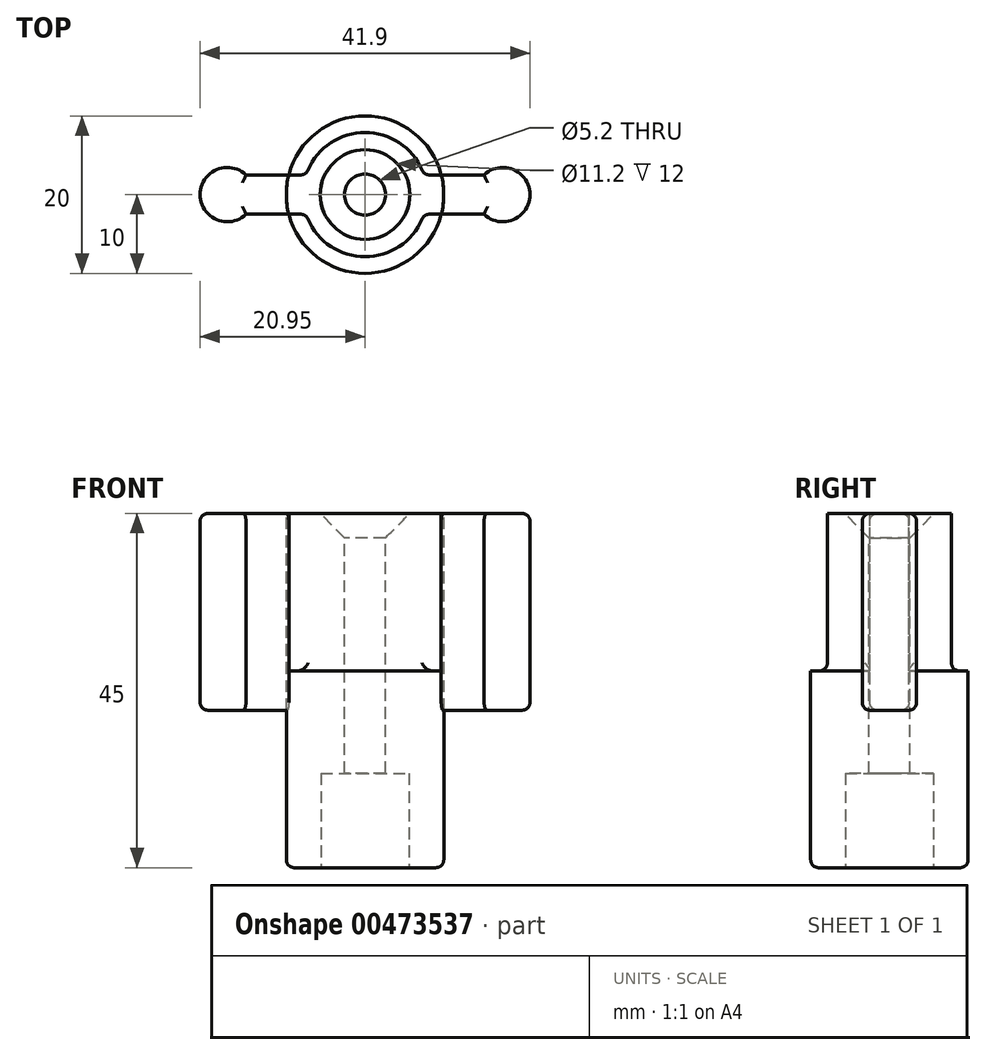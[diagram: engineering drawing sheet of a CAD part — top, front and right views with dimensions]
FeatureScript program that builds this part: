
annotation { "Feature Type Name" : "Feature", "Feature Type Description" : "" }
export const myFeature = defineFeature(function(context is Context, id is Id, definition is map)
    precondition{}
    {
        {
            var Q0;
            Q0=qCreatedBy(makeId("Top.planeOp"),FACE);
            var sketch = newSketch(context, id + "F0", { "sketchPlane" : qUnion([Q0])});
            skCircle(sketch, "E0", {"center": v(0, 0) * mm, "radius": 10 * mm});
            skSolve(sketch);
        }
        {
            var Q0;
            Q0=makeQuery(id+"F0.imprint","IMPRINT",FACE,{"disambiguationData":[TD([[makeQuery(id+"F0.imprint","IMPRINT",EDGE,{"derivedFrom":sQuery(id+"F0.wireOp",EDGE,"E0")}),1.0]])]});
            extrude(context, id + "F1", {"entities" : qUnion([Q0]), "depth" : 45 * mm, "offsetDistance" : 25 * mm, "symmetric" : true});
        }
        {
            var Q0;
            Q0=makeQuery(id+"F1.opExtrude","CAP_FACE",FACE,{"disambiguationData":[OSD([sQuery(id+"F0.wireOp",EDGE,"E0")])],"isStart":false});
            var sketch = newSketch(context, id + "F2", { "sketchPlane" : qUnion([Q0])});
            skLineSegment(sketch, "E1.bottom", {"start": v(17.5, -2.5) * mm, "end": v(-17.5, -2.5) * mm});
            skLineSegment(sketch, "E1.top", {"start": v(17.5, 2.5) * mm, "end": v(-17.5, 2.5) * mm});
            skLineSegment(sketch, "E1.left", {"start": v(17.5, -2.5) * mm, "end": v(17.5, 2.5) * mm});
            skLineSegment(sketch, "E1.right", {"start": v(-17.5, -2.5) * mm, "end": v(-17.5, 2.5) * mm});
            skPoint(sketch, "E1.middle", {"position": v(0, 0) * mm});
            skCircle(sketch, "E2", {"center": v(0, 0) * mm, "radius": 7.89 * mm});
            skCircle(sketch, "E3", {"center": v(-17.5, 0) * mm, "radius": 3.45 * mm});
            skCircle(sketch, "E4", {"center": v(17.5, 0) * mm, "radius": 3.45 * mm});
            skSolve(sketch);
        }
        {
            var Q0;
            {var subQ0=sQuery(id+"F2.wireOp",EDGE,"E2");var subQ1=sQuery(id+"F2.wireOp",EDGE,"E1.top");var subQ2=makeQuery(id+"F2.imprint","INTERSECT",VERTEX,{"disambiguationData":[OD(0.0)],"derivedFrom":[subQ1,subQ0]});Q0=makeQuery(id+"F2.imprint","IMPRINT",FACE,{"disambiguationData":[TD([[makeQuery(id+"F2.imprint","IMPRINT",EDGE,{"disambiguationData":[TD([[subQ2,1.0]])],"derivedFrom":subQ1}),-1.0]])]});}
            var Q1;
            {var subQ0=sQuery(id+"F2.wireOp",EDGE,"E2");var subQ1=sQuery(id+"F2.wireOp",EDGE,"E1.bottom");var subQ2=makeQuery(id+"F2.imprint","INTERSECT",VERTEX,{"disambiguationData":[OD(0.0)],"derivedFrom":[subQ1,subQ0]});Q1=makeQuery(id+"F2.imprint","IMPRINT",FACE,{"disambiguationData":[TD([[makeQuery(id+"F2.imprint","IMPRINT",EDGE,{"disambiguationData":[TD([[subQ2,1.0]])],"derivedFrom":subQ1}),1.0]])]});}
            extrude(context, id + "F3", {"entities" : qUnion([Q0, Q1]), "operationType" : NewBodyOperationType.REMOVE, "oppositeDirection" : true, "depth" : 20 * mm, "offsetDistance" : 25 * mm});
        }
        {
            var Q0;
            {var subQ0=sQuery(id+"F2.wireOp",EDGE,"E1.left");Q0=makeQuery(id+"F2.imprint","IMPRINT",FACE,{"disambiguationData":[TD([[makeQuery(id+"F2.imprint","IMPRINT",EDGE,{"derivedFrom":subQ0}),1.0]])]});}
            var Q1;
            {var subQ0=sQuery(id+"F2.wireOp",EDGE,"E1.right");Q1=makeQuery(id+"F2.imprint","IMPRINT",FACE,{"disambiguationData":[TD([[makeQuery(id+"F2.imprint","IMPRINT",EDGE,{"derivedFrom":subQ0}),-1.0]])]});}
            var Q2;
            {var subQ0=sQuery(id+"F2.wireOp",EDGE,"E4");var subQ1=sQuery(id+"F2.wireOp",EDGE,"E1.bottom");var subQ2=makeQuery(id+"F2.imprint","INTERSECT",VERTEX,{"derivedFrom":[subQ1,subQ0]});Q2=makeQuery(id+"F2.imprint","IMPRINT",FACE,{"disambiguationData":[TD([[makeQuery(id+"F2.imprint","IMPRINT",EDGE,{"disambiguationData":[TD([[subQ2,-1.0]])],"derivedFrom":subQ1}),-1.0]])]});}
            var Q3;
            {var subQ0=sQuery(id+"F2.wireOp",EDGE,"E1.left");Q3=makeQuery(id+"F2.imprint","IMPRINT",FACE,{"disambiguationData":[TD([[makeQuery(id+"F2.imprint","IMPRINT",EDGE,{"derivedFrom":subQ0}),-1.0]])]});}
            var Q4;
            {var subQ0=sQuery(id+"F2.wireOp",EDGE,"E3");var subQ1=sQuery(id+"F2.wireOp",EDGE,"E1.bottom");var subQ2=makeQuery(id+"F2.imprint","INTERSECT",VERTEX,{"derivedFrom":[subQ1,subQ0]});Q4=makeQuery(id+"F2.imprint","IMPRINT",FACE,{"disambiguationData":[TD([[makeQuery(id+"F2.imprint","IMPRINT",EDGE,{"disambiguationData":[TD([[subQ2,1.0]])],"derivedFrom":subQ1}),-1.0]])]});}
            var Q5;
            {var subQ0=sQuery(id+"F2.wireOp",EDGE,"E1.right");Q5=makeQuery(id+"F2.imprint","IMPRINT",FACE,{"disambiguationData":[TD([[makeQuery(id+"F2.imprint","IMPRINT",EDGE,{"derivedFrom":subQ0}),1.0]])]});}
            extrude(context, id + "F4", {"entities" : qUnion([Q0, Q1, Q2, Q3, Q4, Q5]), "oppositeDirection" : true, "depth" : 25 * mm, "offsetDistance" : 25 * mm});
        }
        {
            var Q0;
            {var subQ0=sQuery(id+"F2.wireOp",EDGE,"E1.top");Q0=makeQuery(id+"F4.opExtrude","CAP_EDGE",EDGE,{"disambiguationData":[OSD([subQ0]),TDD([makeQuery(id+"F2.imprint","IMPRINT",EDGE,{"disambiguationData":[TD([[makeQuery(id+"F2.imprint","INTERSECT",VERTEX,{"derivedFrom":[subQ0,sQuery(id+"F2.wireOp",EDGE,"E3")]}),1.0]])],"derivedFrom":subQ0})])],"isStart":true});}
            var Q1;
            {var subQ0=sQuery(id+"F2.wireOp",EDGE,"E2");var subQ1=sQuery(id+"F2.wireOp",EDGE,"E1.top");Q1=makeQuery(id+"F3.boolean.opBoolean","COPY",EDGE,{"derivedFrom":makeQuery(id+"F3.opExtrude","CAP_EDGE",EDGE,{"disambiguationData":[OSD([subQ0]),TDD([makeQuery(id+"F2.imprint","IMPRINT",EDGE,{"disambiguationData":[TD([[makeQuery(id+"F2.imprint","INTERSECT",VERTEX,{"disambiguationData":[OD(0.0)],"derivedFrom":[subQ1,subQ0]}),-1.0]])],"derivedFrom":subQ0})])],"isStart":true})});}
            var Q2;
            {var subQ0=sQuery(id+"F2.wireOp",EDGE,"E2");var subQ1=sQuery(id+"F2.wireOp",EDGE,"E1.bottom");Q2=makeQuery(id+"F3.boolean.opBoolean","COPY",EDGE,{"derivedFrom":makeQuery(id+"F3.opExtrude","CAP_EDGE",EDGE,{"disambiguationData":[OSD([subQ0]),TDD([makeQuery(id+"F2.imprint","IMPRINT",EDGE,{"disambiguationData":[TD([[makeQuery(id+"F2.imprint","INTERSECT",VERTEX,{"disambiguationData":[OD(0.0)],"derivedFrom":[subQ1,subQ0]}),1.0]])],"derivedFrom":subQ0})])],"isStart":true})});}
            var Q3;
            {var subQ0=sQuery(id+"F2.wireOp",EDGE,"E1.bottom");Q3=makeQuery(id+"F3.boolean.opBoolean","COPY",EDGE,{"derivedFrom":makeQuery(id+"F3.opExtrude","CAP_EDGE",EDGE,{"disambiguationData":[OSD([subQ0]),TDD([makeQuery(id+"F2.imprint","IMPRINT",EDGE,{"disambiguationData":[TD([[makeQuery(id+"F2.imprint","INTERSECT",VERTEX,{"disambiguationData":[OD(1.0)],"derivedFrom":[subQ0,sQuery(id+"F2.wireOp",EDGE,"E2")]}),-1.0]])],"derivedFrom":subQ0})])],"isStart":true})});}
            var Q4;
            {var subQ0=sQuery(id+"F2.wireOp",EDGE,"E1.bottom");Q4=makeQuery(id+"F4.opExtrude","CAP_EDGE",EDGE,{"disambiguationData":[OSD([subQ0]),TDD([makeQuery(id+"F2.imprint","IMPRINT",EDGE,{"disambiguationData":[TD([[makeQuery(id+"F2.imprint","INTERSECT",VERTEX,{"derivedFrom":[subQ0,sQuery(id+"F2.wireOp",EDGE,"E3")]}),1.0]])],"derivedFrom":subQ0})])],"isStart":true});}
            var Q5;
            {var subQ0=sQuery(id+"F2.wireOp",EDGE,"E1.bottom");Q5=makeQuery(id+"F3.boolean.opBoolean","COPY",EDGE,{"derivedFrom":makeQuery(id+"F3.opExtrude","CAP_EDGE",EDGE,{"disambiguationData":[OSD([subQ0]),TDD([makeQuery(id+"F2.imprint","IMPRINT",EDGE,{"disambiguationData":[TD([[makeQuery(id+"F2.imprint","INTERSECT",VERTEX,{"disambiguationData":[OD(0.0)],"derivedFrom":[subQ0,sQuery(id+"F2.wireOp",EDGE,"E2")]}),1.0]])],"derivedFrom":subQ0})])],"isStart":true})});}
            var Q6;
            {var subQ0=sQuery(id+"F2.wireOp",EDGE,"E1.bottom");Q6=makeQuery(id+"F4.opExtrude","CAP_EDGE",EDGE,{"disambiguationData":[OSD([subQ0]),TDD([makeQuery(id+"F2.imprint","IMPRINT",EDGE,{"disambiguationData":[TD([[makeQuery(id+"F2.imprint","INTERSECT",VERTEX,{"derivedFrom":[subQ0,sQuery(id+"F2.wireOp",EDGE,"E4")]}),-1.0]])],"derivedFrom":subQ0})])],"isStart":true});}
            var Q7;
            {var subQ0=sQuery(id+"F2.wireOp",EDGE,"E1.top");Q7=makeQuery(id+"F3.boolean.opBoolean","COPY",EDGE,{"derivedFrom":makeQuery(id+"F3.opExtrude","CAP_EDGE",EDGE,{"disambiguationData":[OSD([subQ0]),TDD([makeQuery(id+"F2.imprint","IMPRINT",EDGE,{"disambiguationData":[TD([[makeQuery(id+"F2.imprint","INTERSECT",VERTEX,{"disambiguationData":[OD(1.0)],"derivedFrom":[subQ0,sQuery(id+"F2.wireOp",EDGE,"E2")]}),-1.0]])],"derivedFrom":subQ0})])],"isStart":true})});}
            var Q8;
            {var subQ0=sQuery(id+"F2.wireOp",EDGE,"E1.top");Q8=makeQuery(id+"F3.boolean.opBoolean","COPY",EDGE,{"derivedFrom":makeQuery(id+"F3.opExtrude","CAP_EDGE",EDGE,{"disambiguationData":[OSD([subQ0]),TDD([makeQuery(id+"F2.imprint","IMPRINT",EDGE,{"disambiguationData":[TD([[makeQuery(id+"F2.imprint","INTERSECT",VERTEX,{"disambiguationData":[OD(0.0)],"derivedFrom":[subQ0,sQuery(id+"F2.wireOp",EDGE,"E2")]}),1.0]])],"derivedFrom":subQ0})])],"isStart":true})});}
            var Q9;
            {var subQ0=sQuery(id+"F2.wireOp",EDGE,"E1.top");Q9=makeQuery(id+"F4.opExtrude","CAP_EDGE",EDGE,{"disambiguationData":[OSD([subQ0]),TDD([makeQuery(id+"F2.imprint","IMPRINT",EDGE,{"disambiguationData":[TD([[makeQuery(id+"F2.imprint","INTERSECT",VERTEX,{"derivedFrom":[subQ0,sQuery(id+"F2.wireOp",EDGE,"E4")]}),-1.0]])],"derivedFrom":subQ0})])],"isStart":true});}
            var Q10;
            {var subQ0=sQuery(id+"F2.wireOp",EDGE,"E2");var subQ1=sQuery(id+"F2.wireOp",EDGE,"E1.top");Q10=makeQuery(id+"F3.boolean.opBoolean","COPY",EDGE,{"derivedFrom":makeQuery(id+"F3.opExtrude","SWEPT_EDGE",EDGE,{"disambiguationData":[OSD([subQ1,subQ0]),TDD([makeQuery(id+"F2.imprint","INTERSECT",VERTEX,{"disambiguationData":[OD(0.0)],"derivedFrom":[subQ1,subQ0]})])]})});}
            var Q11;
            {var subQ0=sQuery(id+"F2.wireOp",EDGE,"E2");var subQ1=sQuery(id+"F2.wireOp",EDGE,"E1.top");Q11=makeQuery(id+"F3.boolean.opBoolean","COPY",EDGE,{"derivedFrom":makeQuery(id+"F3.opExtrude","SWEPT_EDGE",EDGE,{"disambiguationData":[OSD([subQ1,subQ0]),TDD([makeQuery(id+"F2.imprint","INTERSECT",VERTEX,{"disambiguationData":[OD(1.0)],"derivedFrom":[subQ1,subQ0]})])]})});}
            var Q12;
            {var subQ0=sQuery(id+"F2.wireOp",EDGE,"E2");var subQ1=sQuery(id+"F2.wireOp",EDGE,"E1.top");Q12=makeQuery(id+"F3.boolean.opBoolean","COPY",EDGE,{"derivedFrom":makeQuery(id+"F3.opExtrude","CAP_EDGE",EDGE,{"disambiguationData":[OSD([subQ0]),TDD([makeQuery(id+"F2.imprint","IMPRINT",EDGE,{"disambiguationData":[TD([[makeQuery(id+"F2.imprint","INTERSECT",VERTEX,{"disambiguationData":[OD(0.0)],"derivedFrom":[subQ1,subQ0]}),-1.0]])],"derivedFrom":subQ0})])],"isStart":false})});}
            var Q13;
            {var subQ0=sQuery(id+"F2.wireOp",EDGE,"E1.top");var subQ1=sQuery(id+"F0.wireOp",EDGE,"E0");var subQ2=makeQuery(id+"F1.opExtrude","CAP_EDGE",EDGE,{"disambiguationData":[OSD([subQ1])],"isStart":false});Q13=makeQuery(id+"F3.boolean.opBoolean","COPY",EDGE,{"derivedFrom":makeQuery(id+"F3.opExtrude","CAP_EDGE",EDGE,{"disambiguationData":[OSD([subQ1]),TDD([makeQuery(id+"F2.imprint","IMPRINT",EDGE,{"disambiguationData":[TD([[makeQuery(id+"F2.imprint","INTERSECT",VERTEX,{"disambiguationData":[OD(0.0)],"derivedFrom":[subQ2,subQ0]}),-1.0]])],"derivedFrom":subQ2})])],"isStart":false})});}
            var Q14;
            {var subQ0=sQuery(id+"F2.wireOp",EDGE,"E2");var subQ1=sQuery(id+"F2.wireOp",EDGE,"E1.bottom");Q14=makeQuery(id+"F3.boolean.opBoolean","COPY",EDGE,{"derivedFrom":makeQuery(id+"F3.opExtrude","SWEPT_EDGE",EDGE,{"disambiguationData":[OSD([subQ1,subQ0]),TDD([makeQuery(id+"F2.imprint","INTERSECT",VERTEX,{"disambiguationData":[OD(0.0)],"derivedFrom":[subQ1,subQ0]})])]})});}
            var Q15;
            {var subQ0=sQuery(id+"F2.wireOp",EDGE,"E2");var subQ1=sQuery(id+"F2.wireOp",EDGE,"E1.bottom");Q15=makeQuery(id+"F3.boolean.opBoolean","COPY",EDGE,{"derivedFrom":makeQuery(id+"F3.opExtrude","CAP_EDGE",EDGE,{"disambiguationData":[OSD([subQ0]),TDD([makeQuery(id+"F2.imprint","IMPRINT",EDGE,{"disambiguationData":[TD([[makeQuery(id+"F2.imprint","INTERSECT",VERTEX,{"disambiguationData":[OD(0.0)],"derivedFrom":[subQ1,subQ0]}),1.0]])],"derivedFrom":subQ0})])],"isStart":false})});}
            var Q16;
            {var subQ0=sQuery(id+"F2.wireOp",EDGE,"E1.bottom");var subQ1=sQuery(id+"F0.wireOp",EDGE,"E0");var subQ2=makeQuery(id+"F1.opExtrude","CAP_EDGE",EDGE,{"disambiguationData":[OSD([subQ1])],"isStart":false});Q16=makeQuery(id+"F3.boolean.opBoolean","COPY",EDGE,{"derivedFrom":makeQuery(id+"F3.opExtrude","CAP_EDGE",EDGE,{"disambiguationData":[OSD([subQ1]),TDD([makeQuery(id+"F2.imprint","IMPRINT",EDGE,{"disambiguationData":[TD([[makeQuery(id+"F2.imprint","INTERSECT",VERTEX,{"disambiguationData":[OD(0.0)],"derivedFrom":[subQ2,subQ0]}),1.0]])],"derivedFrom":subQ2})])],"isStart":false})});}
            var Q17;
            {var subQ0=sQuery(id+"F2.wireOp",EDGE,"E2");var subQ1=sQuery(id+"F2.wireOp",EDGE,"E1.bottom");Q17=makeQuery(id+"F3.boolean.opBoolean","COPY",EDGE,{"derivedFrom":makeQuery(id+"F3.opExtrude","SWEPT_EDGE",EDGE,{"disambiguationData":[OSD([subQ1,subQ0]),TDD([makeQuery(id+"F2.imprint","INTERSECT",VERTEX,{"disambiguationData":[OD(1.0)],"derivedFrom":[subQ1,subQ0]})])]})});}
            var Q18;
            {var subQ0=sQuery(id+"F2.wireOp",EDGE,"E1.bottom");Q18=makeQuery(id+"F4.opExtrude","CAP_EDGE",EDGE,{"disambiguationData":[OSD([subQ0]),TDD([makeQuery(id+"F2.imprint","IMPRINT",EDGE,{"disambiguationData":[TD([[makeQuery(id+"F2.imprint","INTERSECT",VERTEX,{"derivedFrom":[subQ0,sQuery(id+"F2.wireOp",EDGE,"E3")]}),1.0]])],"derivedFrom":subQ0})])],"isStart":false});}
            var Q19;
            {var subQ0=sQuery(id+"F2.wireOp",EDGE,"E1.top");Q19=makeQuery(id+"F4.opExtrude","CAP_EDGE",EDGE,{"disambiguationData":[OSD([subQ0]),TDD([makeQuery(id+"F2.imprint","IMPRINT",EDGE,{"disambiguationData":[TD([[makeQuery(id+"F2.imprint","INTERSECT",VERTEX,{"derivedFrom":[subQ0,sQuery(id+"F2.wireOp",EDGE,"E3")]}),1.0]])],"derivedFrom":subQ0})])],"isStart":false});}
            var Q20;
            {var subQ0=sQuery(id+"F2.wireOp",EDGE,"E1.bottom");Q20=makeQuery(id+"F4.opExtrude","CAP_EDGE",EDGE,{"disambiguationData":[OSD([subQ0]),TDD([makeQuery(id+"F2.imprint","IMPRINT",EDGE,{"disambiguationData":[TD([[makeQuery(id+"F2.imprint","INTERSECT",VERTEX,{"derivedFrom":[subQ0,sQuery(id+"F2.wireOp",EDGE,"E4")]}),-1.0]])],"derivedFrom":subQ0})])],"isStart":false});}
            var Q21;
            {var subQ0=sQuery(id+"F2.wireOp",EDGE,"E1.top");Q21=makeQuery(id+"F4.opExtrude","CAP_EDGE",EDGE,{"disambiguationData":[OSD([subQ0]),TDD([makeQuery(id+"F2.imprint","IMPRINT",EDGE,{"disambiguationData":[TD([[makeQuery(id+"F2.imprint","INTERSECT",VERTEX,{"derivedFrom":[subQ0,sQuery(id+"F2.wireOp",EDGE,"E4")]}),-1.0]])],"derivedFrom":subQ0})])],"isStart":false});}
            fillet(context, id + "F5", {"entities" : qUnion([Q0, Q1, Q2, Q3, Q4, Q5, Q6, Q7, Q8, Q9, Q10, Q11, Q12, Q13, Q14, Q15, Q16, Q17, Q18, Q19, Q20, Q21]), "radius" : 1 * mm, "allowEdgeOverflow" : false});
        }
        {
            var Q0;
            Q0=makeQuery(id+"F4.opExtrude","CAP_EDGE",EDGE,{"disambiguationData":[OSD([sQuery(id+"F2.wireOp",EDGE,"E4")])],"isStart":true});
            var Q1;
            Q1=makeQuery(id+"F4.opExtrude","CAP_EDGE",EDGE,{"disambiguationData":[OSD([sQuery(id+"F2.wireOp",EDGE,"E3")])],"isStart":true});
            var Q2;
            Q2=makeQuery(id+"F4.opExtrude","CAP_EDGE",EDGE,{"disambiguationData":[OSD([sQuery(id+"F2.wireOp",EDGE,"E3")])],"isStart":false});
            var Q3;
            Q3=makeQuery(id+"F4.opExtrude","CAP_EDGE",EDGE,{"disambiguationData":[OSD([sQuery(id+"F2.wireOp",EDGE,"E4")])],"isStart":false});
            fillet(context, id + "F6", {"entities" : qUnion([Q0, Q1, Q2, Q3]), "radius" : 1 * mm, "tangentPropagation" : true, "allowEdgeOverflow" : false});
        }
        {
            var Q0;
            Q0=sQuery(id+"F2.wireOp",VERTEX,"E1.middle");
            var Q1;
            Q1=makeQuery(id+"F1.opExtrude","SWEPT_BODY",BODY,{"disambiguationData":[OSD([sQuery(id+"F0.wireOp",EDGE,"E0")])]});
            hole(context, id + "F7", {"style" : HoleStyle.C_SINK, "endStyle" : HoleEndStyle.THROUGH, "holeDiameter" : 5.2 * mm, "cSinkDiameter" : 11.4 * mm, "cSinkAngle" : 90 * degree, "majorDiameter" : 5 * mm, "isTappedThrough" : true, "tappedDepth" : 12 * mm, "tapClearance" : 3, "locations" : qUnion([Q0]), "scope" : qUnion([Q1])});
        }
        {
            var Q0;
            Q0=makeQuery(id+"F1.opExtrude","CAP_FACE",FACE,{"disambiguationData":[OSD([sQuery(id+"F0.wireOp",EDGE,"E0")])],"isStart":true});
            var sketch = newSketch(context, id + "F8", { "sketchPlane" : qUnion([Q0])});
            skCircle(sketch, "E5", {"center": v(0, 0) * mm, "radius": 5.6 * mm});
            skSolve(sketch);
        }
        {
            var Q0;
            Q0=makeQuery(id+"F8.imprint","IMPRINT",FACE,{"disambiguationData":[TD([[makeQuery(id+"F8.imprint","IMPRINT",EDGE,{"derivedFrom":sQuery(id+"F8.wireOp",EDGE,"E5")}),1.0]])]});
            extrude(context, id + "F9", {"entities" : qUnion([Q0]), "operationType" : NewBodyOperationType.REMOVE, "oppositeDirection" : true, "depth" : 12 * mm, "offsetDistance" : 25 * mm});
        }
        {
            var Q0;
            Q0=makeQuery(id+"F1.opExtrude","CAP_EDGE",EDGE,{"disambiguationData":[OSD([sQuery(id+"F0.wireOp",EDGE,"E0")])],"isStart":true});
            fillet(context, id + "F10", {"entities" : qUnion([Q0]), "radius" : 1 * mm, "tangentPropagation" : true, "allowEdgeOverflow" : false});
        }
    });
